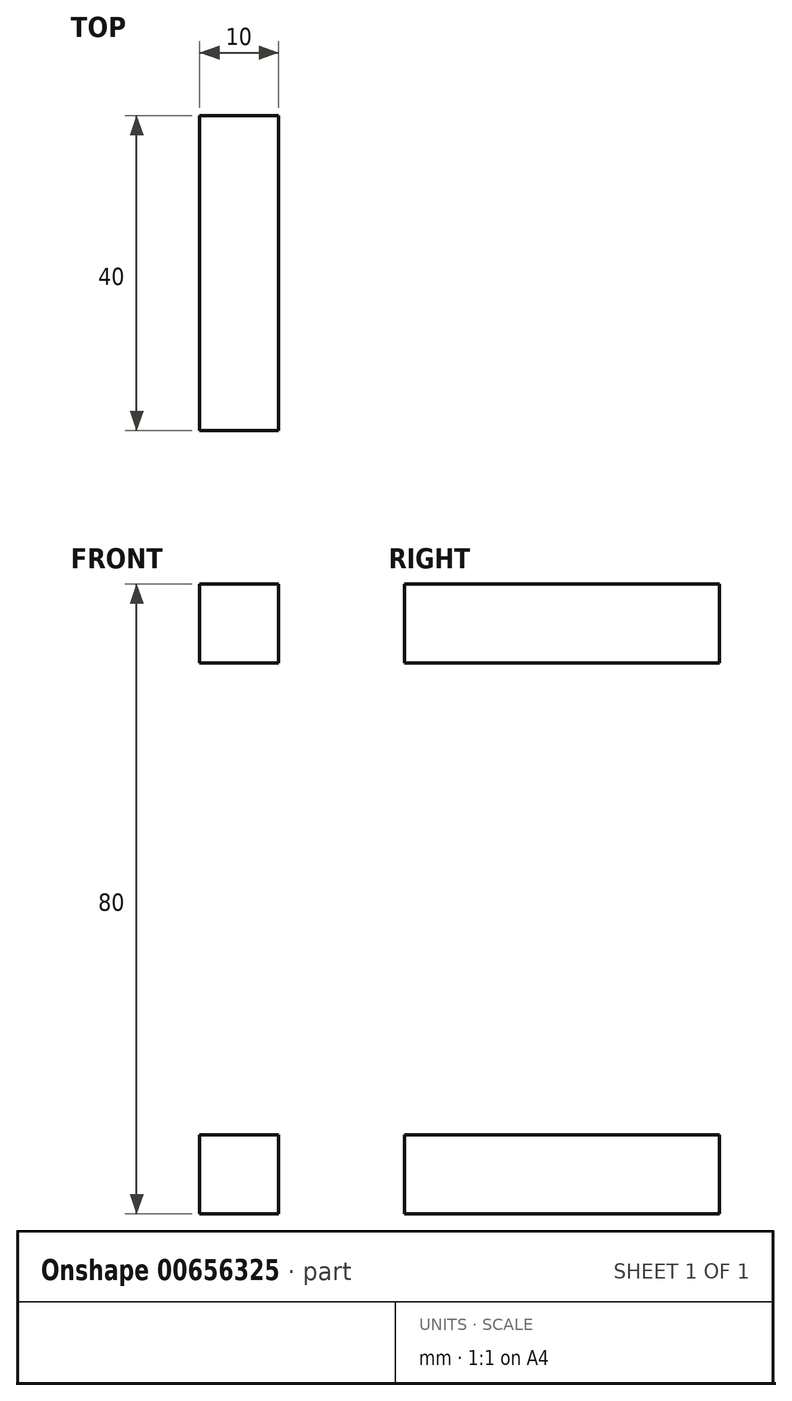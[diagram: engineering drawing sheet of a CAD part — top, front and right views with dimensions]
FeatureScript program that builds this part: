
annotation { "Feature Type Name" : "Feature", "Feature Type Description" : "" }
export const myFeature = defineFeature(function(context is Context, id is Id, definition is map)
    precondition{}
    {
        {
            var Q0;
            Q0=qCreatedBy(makeId("Right.planeOp"),FACE);
            var sketch = newSketch(context, id + "F0", { "sketchPlane" : qUnion([Q0])});
            skLineSegment(sketch, "E0.bottom", {"start": v(0, 0) * mm, "end": v(-40, 0) * mm});
            skLineSegment(sketch, "E0.top", {"start": v(0, 10) * mm, "end": v(-40, 10) * mm});
            skLineSegment(sketch, "E0.left", {"start": v(0, 0) * mm, "end": v(0, 10) * mm});
            skLineSegment(sketch, "E0.right", {"start": v(-40, 0) * mm, "end": v(-40, 10) * mm});
            skLineSegment(sketch, "E1.bottom", {"start": v(0, 10) * mm, "end": v(-10, 10) * mm});
            skLineSegment(sketch, "E1.top", {"start": v(0, 70) * mm, "end": v(-10, 70) * mm});
            skLineSegment(sketch, "E1.left", {"start": v(0, 10) * mm, "end": v(0, 70) * mm});
            skLineSegment(sketch, "E1.right", {"start": v(-10, 10) * mm, "end": v(-10, 70) * mm});
            skLineSegment(sketch, "E2.bottom", {"start": v(0, 70) * mm, "end": v(-40, 70) * mm});
            skLineSegment(sketch, "E2.top", {"start": v(0, 80) * mm, "end": v(-40, 80) * mm});
            skLineSegment(sketch, "E2.left", {"start": v(0, 70) * mm, "end": v(0, 80) * mm});
            skLineSegment(sketch, "E2.right", {"start": v(-40, 70) * mm, "end": v(-40, 80) * mm});
            skSolve(sketch);
        }
        {
            var Q0;
            Q0=makeQuery(id+"F0.imprint","IMPRINT",FACE,{"disambiguationData":[TD([[makeQuery(id+"F0.imprint","IMPRINT",EDGE,{"derivedFrom":sQuery(id+"F0.wireOp",EDGE,"E2.top")}),1.0]])]});
            var Q1;
            Q1=makeQuery(id+"F0.imprint","IMPRINT",FACE,{"disambiguationData":[TD([[makeQuery(id+"F0.imprint","IMPRINT",EDGE,{"derivedFrom":sQuery(id+"F0.wireOp",EDGE,"E1.bottom")}),-1.0]])]});
            var Q2;
            Q2=makeQuery(id+"F0.imprint","IMPRINT",FACE,{"disambiguationData":[TD([[makeQuery(id+"F0.imprint","IMPRINT",EDGE,{"derivedFrom":sQuery(id+"F0.wireOp",EDGE,"E0.bottom")}),-1.0]])]});
            extrude(context, id + "F1", {"entities" : qUnion([Q0, Q1, Q2]), "depth" : 10 * mm, "offsetDistance" : 25 * mm});
        }
    });
